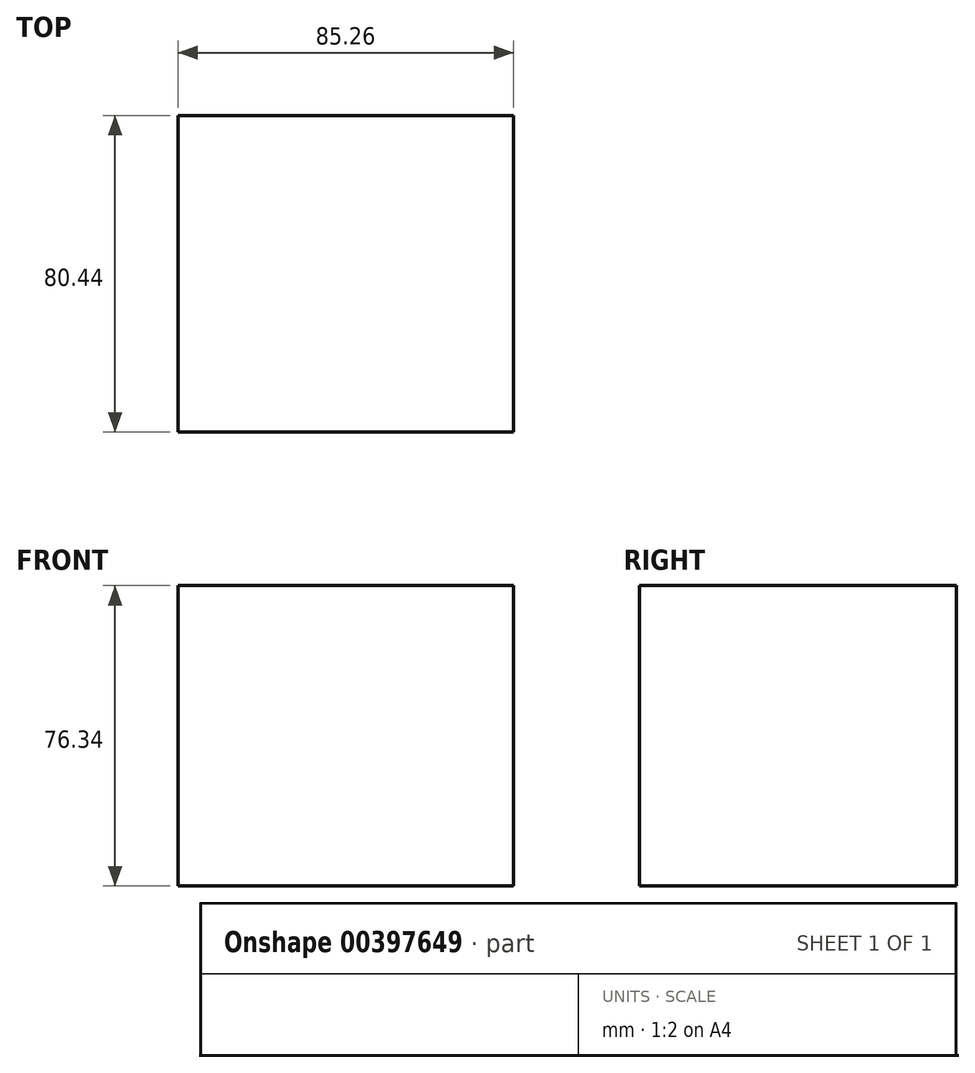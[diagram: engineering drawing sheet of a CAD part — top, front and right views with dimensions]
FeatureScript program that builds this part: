
annotation { "Feature Type Name" : "Feature", "Feature Type Description" : "" }
export const myFeature = defineFeature(function(context is Context, id is Id, definition is map)
    precondition{}
    {
        {
            var Q0;
            Q0=qCreatedBy(makeId("Front.planeOp"),FACE);
            var sketch = newSketch(context, id + "F0", { "sketchPlane" : qUnion([Q0])});
            skLineSegment(sketch, "E0.bottom", {"start": v(6.43, 0) * mm, "end": v(-78.83, 0) * mm});
            skLineSegment(sketch, "E0.top", {"start": v(6.43, 76.34) * mm, "end": v(-78.83, 76.34) * mm});
            skLineSegment(sketch, "E0.left", {"start": v(6.43, 0) * mm, "end": v(6.43, 76.34) * mm});
            skLineSegment(sketch, "E0.right", {"start": v(-78.83, 0) * mm, "end": v(-78.83, 76.34) * mm});
            skSolve(sketch);
        }
        {
            var Q0;
            Q0 = qSketchRegion(id + "F0", true);
            extrude(context, id + "F1", {"entities" : qUnion([Q0]), "endBound" : BoundingType.SYMMETRIC, "depth" : 80.44 * mm});
        }
        {
            var Q0;
            Q0=makeQuery(id+"F1.opExtrude","SWEPT_FACE",FACE,{"disambiguationData":[OSD([sQuery(id+"F0.wireOp",EDGE,"E0.right")])]});
            extrude(context, id + "F2", {"entities" : qUnion([Q0]), "operationType" : NewBodyOperationType.ADD, "oppositeDirection" : true, "depth" : 25.4 * mm});
        }
    });
